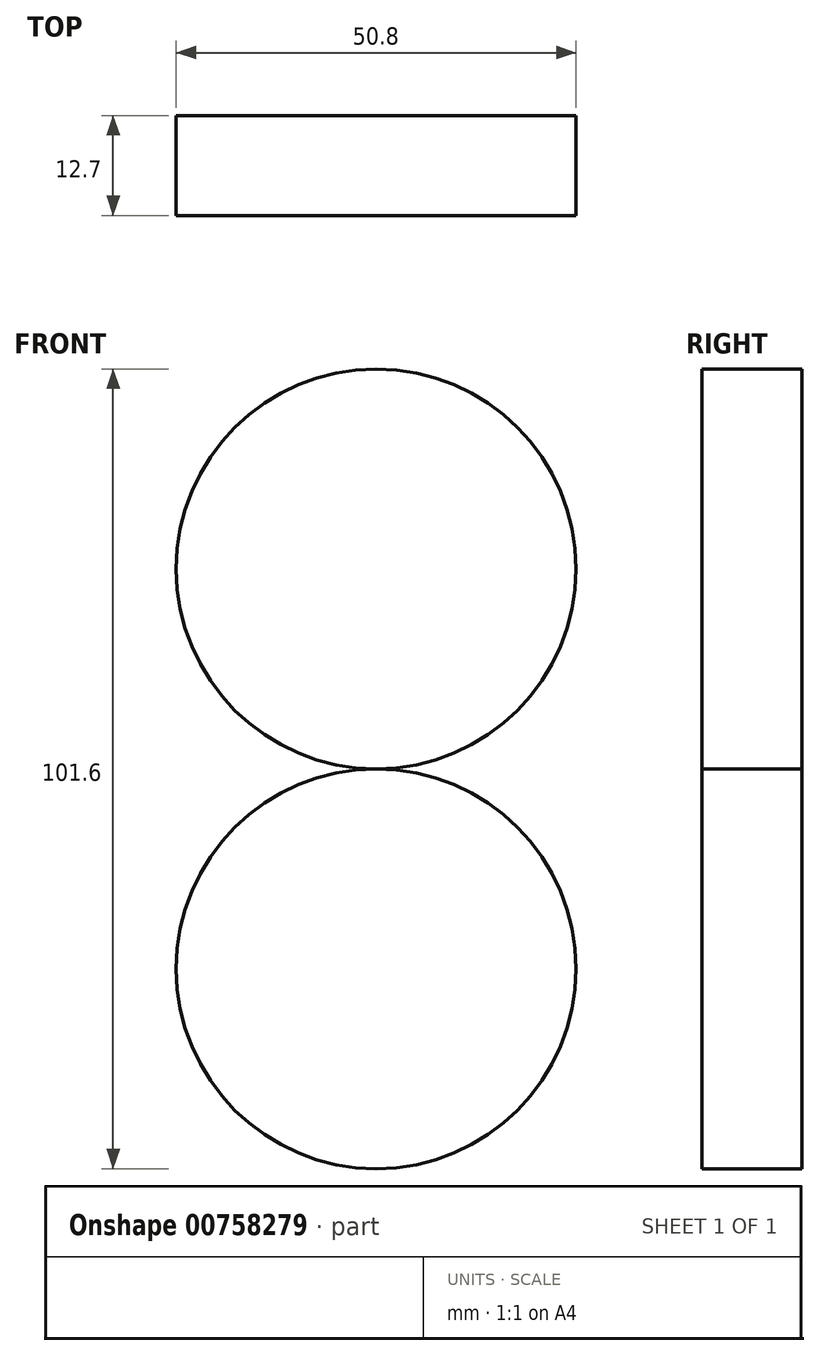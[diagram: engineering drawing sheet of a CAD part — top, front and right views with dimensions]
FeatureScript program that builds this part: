
annotation { "Feature Type Name" : "Feature", "Feature Type Description" : "" }
export const myFeature = defineFeature(function(context is Context, id is Id, definition is map)
    precondition{}
    {
        {
            var Q0;
            Q0=qCreatedBy(makeId("Front.planeOp"),FACE);
            var sketch = newSketch(context, id + "F0", { "sketchPlane" : qUnion([Q0])});
            skCircle(sketch, "E0", {"center": v(-43.42, 38.38) * mm, "radius": 25.4 * mm});
            skCircle(sketch, "E1", {"center": v(-43.42, -12.42) * mm, "radius": 25.4 * mm});
            skSolve(sketch);
        }
        {
            var Q0;
            Q0 = qSketchRegion(id + "F0", true);
            extrude(context, id + "F1", {"entities" : qUnion([Q0]), "depth" : 12.7 * mm, "offsetDistance" : 25.4 * mm});
        }
    });
